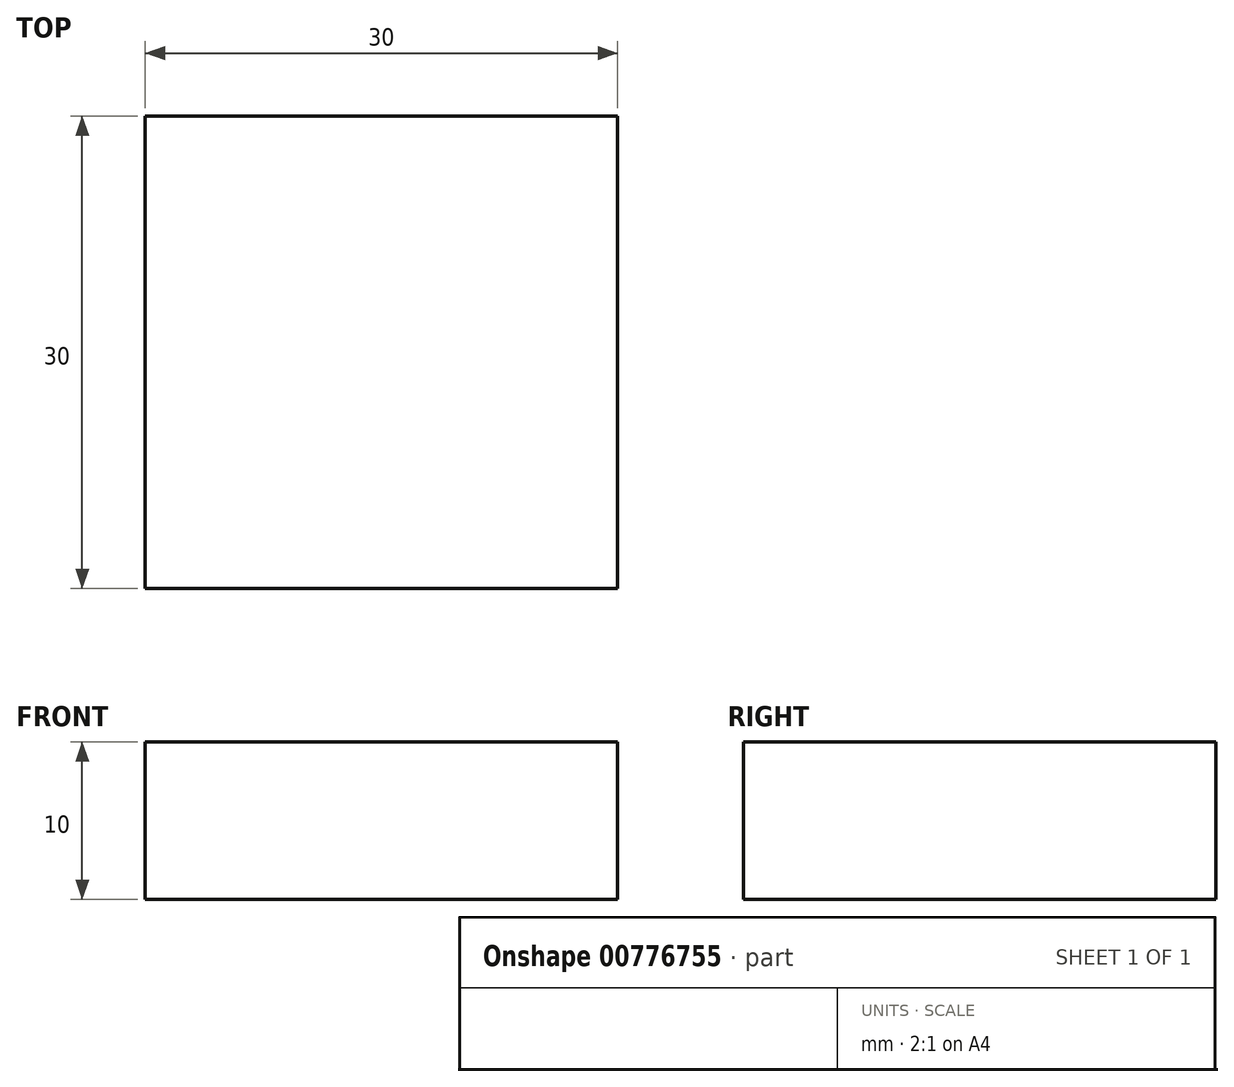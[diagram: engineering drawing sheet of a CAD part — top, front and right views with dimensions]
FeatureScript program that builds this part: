
annotation { "Feature Type Name" : "Feature", "Feature Type Description" : "" }
export const myFeature = defineFeature(function(context is Context, id is Id, definition is map)
    precondition{}
    {
        {
            var Q0;
            Q0=qCreatedBy(makeId("Top.planeOp"),FACE);
            var sketch = newSketch(context, id + "F0", { "sketchPlane" : qUnion([Q0])});
            skLineSegment(sketch, "E0.bottom", {"start": v(0, 0) * mm, "end": v(30, 0) * mm});
            skLineSegment(sketch, "E0.top", {"start": v(0, -30) * mm, "end": v(30, -30) * mm});
            skLineSegment(sketch, "E0.left", {"start": v(0, 0) * mm, "end": v(0, -30) * mm});
            skLineSegment(sketch, "E0.right", {"start": v(30, 0) * mm, "end": v(30, -30) * mm});
            skSolve(sketch);
        }
        {
            var Q0;
            Q0 = qSketchRegion(id + "F0", true);
            extrude(context, id + "F1", {"entities" : qUnion([Q0]), "depth" : 10 * mm, "offsetDistance" : 25 * mm});
        }
    });
